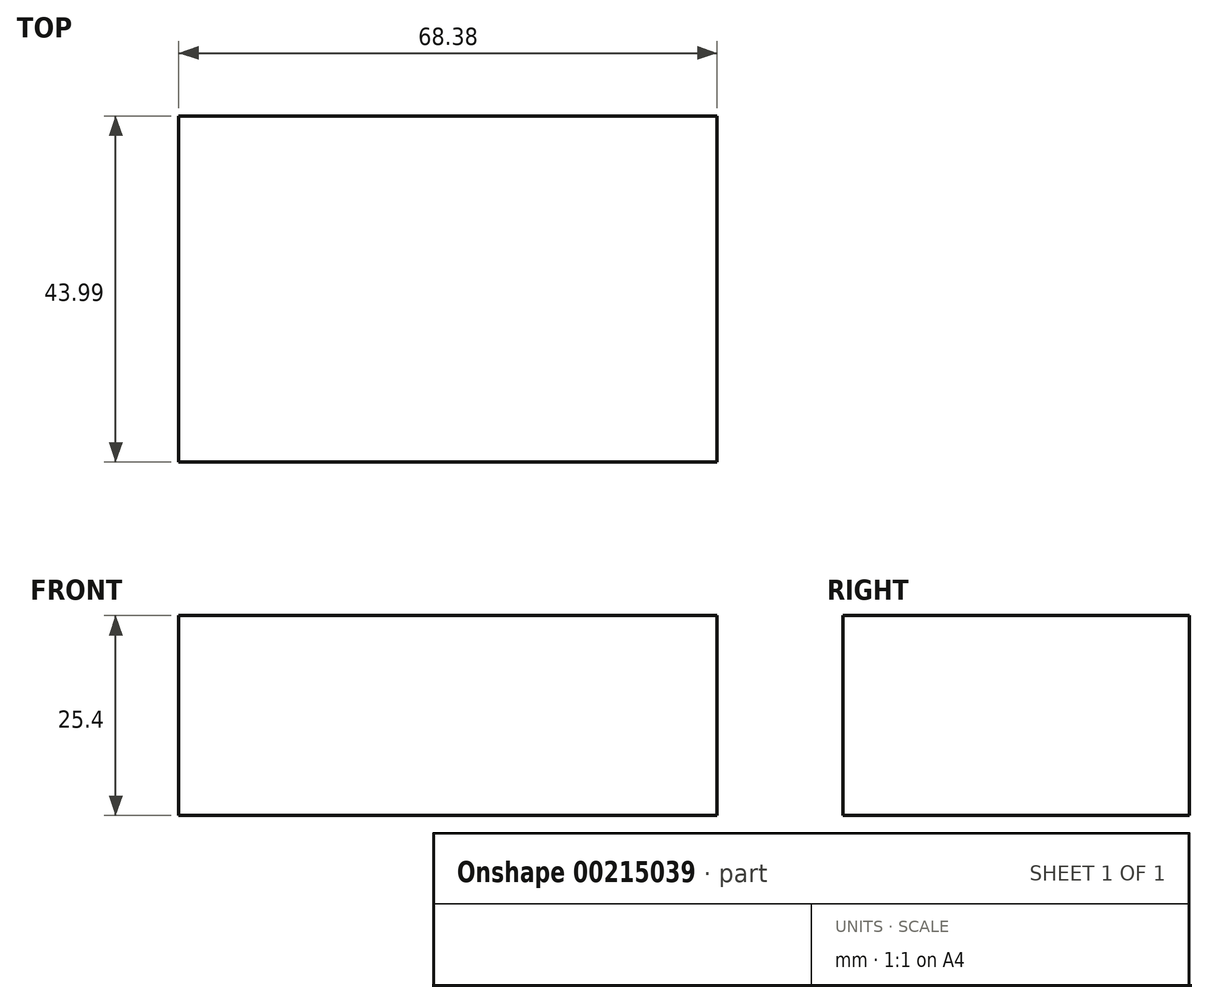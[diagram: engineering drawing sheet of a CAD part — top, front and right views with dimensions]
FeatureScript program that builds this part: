
annotation { "Feature Type Name" : "Feature", "Feature Type Description" : "" }
export const myFeature = defineFeature(function(context is Context, id is Id, definition is map)
    precondition{}
    {
        {
            var Q0;
            Q0=qCreatedBy(makeId("Top.planeOp"),FACE);
            var sketch = newSketch(context, id + "F0", { "sketchPlane" : qUnion([Q0])});
            skLineSegment(sketch, "E0.bottom", {"start": v(-133.59, 19.11) * mm, "end": v(-65.21, 19.11) * mm});
            skLineSegment(sketch, "E0.top", {"start": v(-133.59, -24.88) * mm, "end": v(-65.21, -24.88) * mm});
            skLineSegment(sketch, "E0.left", {"start": v(-133.59, 19.11) * mm, "end": v(-133.59, -24.88) * mm});
            skLineSegment(sketch, "E0.right", {"start": v(-65.21, 19.11) * mm, "end": v(-65.21, -24.88) * mm});
            skSolve(sketch);
        }
        {
            var Q0;
            Q0 = qSketchRegion(id + "F0", true);
            extrude(context, id + "F1", {"entities" : qUnion([Q0]), "depth" : 25.4 * mm});
        }
    });
